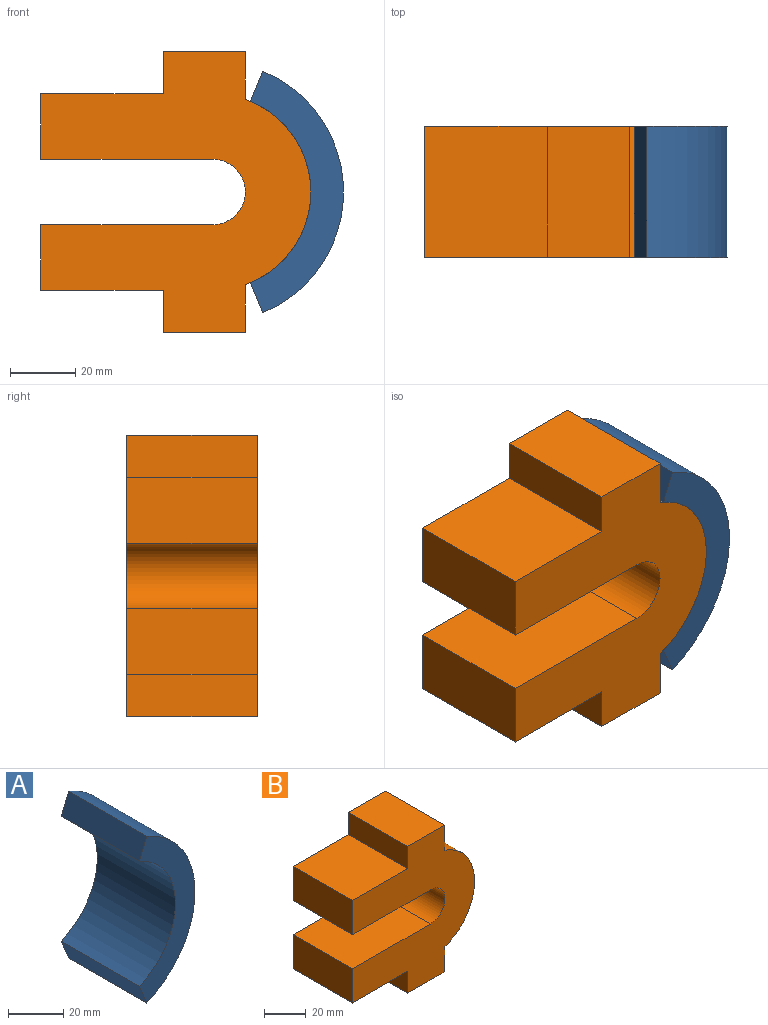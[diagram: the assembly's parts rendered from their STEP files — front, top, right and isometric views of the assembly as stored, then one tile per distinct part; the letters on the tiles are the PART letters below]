
ASSEMBLY  parts=2 mates=1
PART A: 6 faces, bbox 28.5x40x73.9 mm
  f0: plane 40x9.24mm, normal (-0.92,0,0.38), area 400mm2, adj f1,f3,f4,f5
  f1: cylinder r=30mm len=55.43mm, axis (0,-1,0), area 2827.4mm2, adj f0,f2,f4,f5
  f2: plane 40x9.24mm, normal (-0.92,0,-0.38), area 400mm2, adj f1,f3,f4,f5
  f3: cylinder r=40mm len=73.91mm, axis (0,-1,0), area 3769.9mm2, adj f0,f2,f4,f5
  f4: plane 73.91x28.52mm, normal (0,1,0), area 824.7mm2, adj f0,f1,f2,f3
  f5: plane 73.91x28.52mm, normal (0,-1,0), area 824.7mm2, adj f0,f1,f2,f3
PART B: 16 faces, bbox 82.5x40x85.9 mm
  f0: plane 40x20mm, normal (-1,0,0), area 800mm2, adj f1,f13,f14,f15
  f1: plane 52.52x40mm, normal (0,0,-1), area 2100.8mm2, adj f0,f2,f14,f15
  f2: cylinder r=10mm len=40mm, axis (0,1,0), area 1256.6mm2, adj f1,f3,f14,f15
  f3: plane 52.52x40mm, normal (0,0,1), area 2100.8mm2, adj f2,f4,f14,f15
  f4: plane 40x20mm, normal (-1,0,0), area 800mm2, adj f3,f5,f14,f15
  f5: plane 40x37.43mm, normal (0,0,-1), area 1497.3mm2, adj f4,f6,f14,f15
  f6: plane 40x12.93mm, normal (-1,0,0), area 517.1mm2, adj f5,f7,f14,f15
  f7: plane 40x25.09mm, normal (0,0,-1), area 1003.5mm2, adj f6,f8,f14,f15
  f8: plane 40x14.64mm, normal (1,0,0), area 585.7mm2, adj f7,f9,f14,f15
  f9: cylinder r=30mm len=56.57mm, axis (0,1,0), area 2954.3mm2, adj f8,f10,f14,f15
  f10: plane 40x14.64mm, normal (1,0,0), area 585.7mm2, adj f9,f11,f14,f15
  f11: plane 40x25.09mm, normal (0,0,1), area 1003.5mm2, adj f10,f12,f14,f15
  f12: plane 40x12.93mm, normal (-1,0,0), area 517.1mm2, adj f11,f13,f14,f15
  f13: plane 40x37.43mm, normal (0,0,1), area 1497.3mm2, adj f0,f12,f14,f15
  f14: plane 85.86x82.52mm, normal (0,-1,0), area 4017.3mm2, adj f0,f1,f2,f3,f4,f5,f6,f7
  f15: plane 85.86x82.52mm, normal (0,1,0), area 4017.3mm2, adj f0,f1,f2,f3,f4,f5,f6,f7
PLACE A t=(47.54,12.08,-13.58)mm
PLACE B t=(47.54,12.08,-13.58)mm
MATE cylindrical A.f1 <-> B.f9  axis (0,-1,0) through (47.54,-7.92,-13.58)mm
